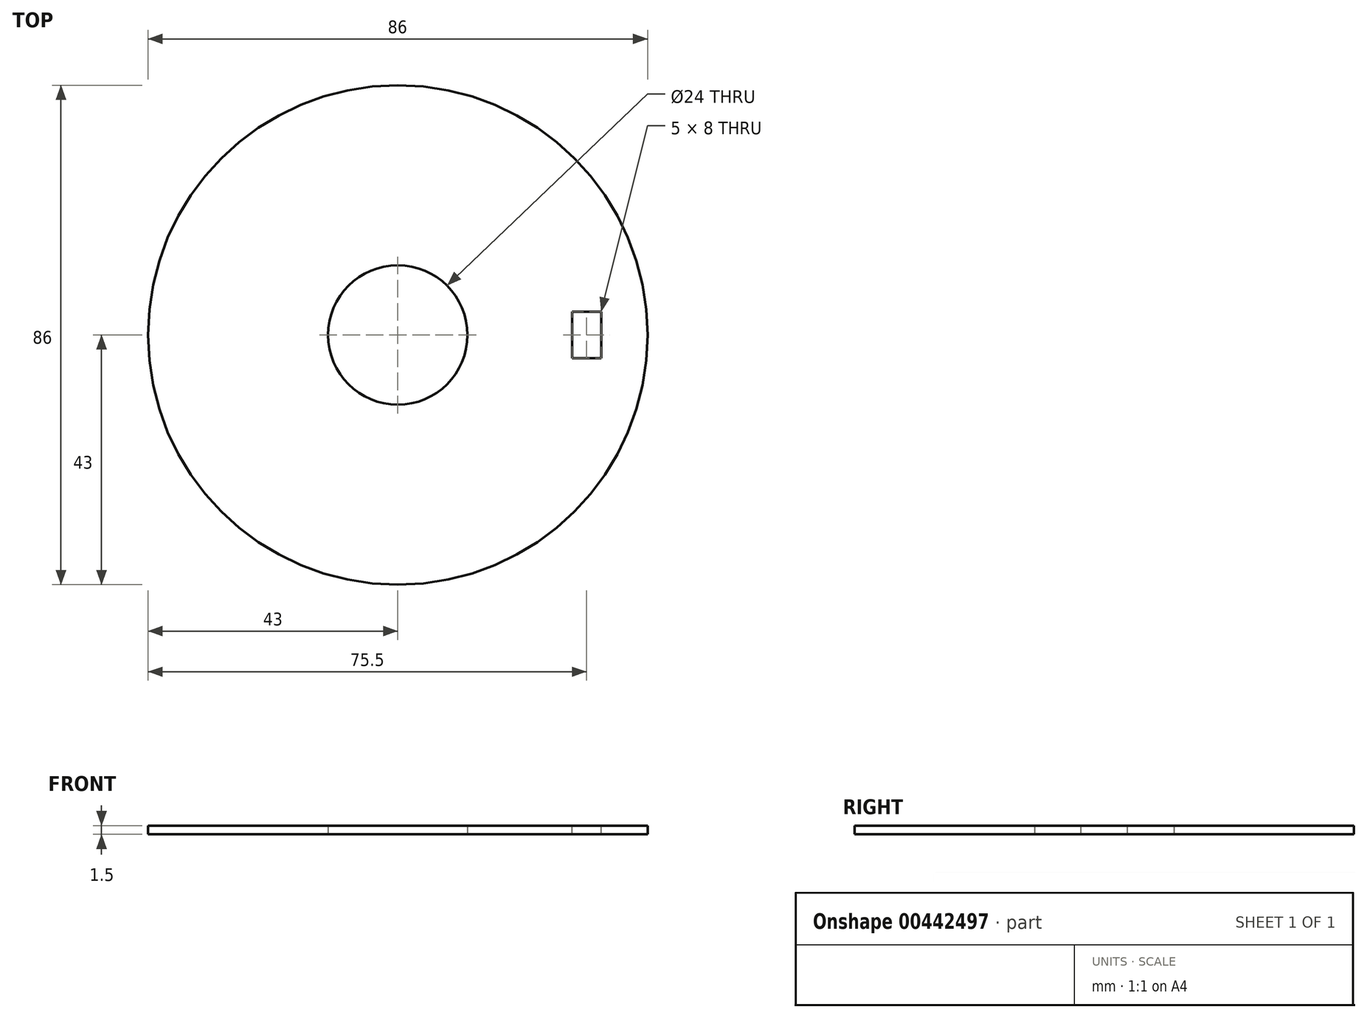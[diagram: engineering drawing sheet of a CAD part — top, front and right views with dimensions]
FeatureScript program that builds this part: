
annotation { "Feature Type Name" : "Feature", "Feature Type Description" : "" }
export const myFeature = defineFeature(function(context is Context, id is Id, definition is map)
    precondition{}
    {
        {
            var Q0;
            Q0=qCreatedBy(makeId("Top.planeOp"),FACE);
            var sketch = newSketch(context, id + "F0", { "sketchPlane" : qUnion([Q0])});
            skCircle(sketch, "E0", {"center": v(0, 0) * mm, "radius": 43 * mm});
            skCircle(sketch, "E1", {"center": v(0, 0) * mm, "radius": 12 * mm});
            skSolve(sketch);
        }
        {
            var Q0;
            Q0=makeQuery(id+"F0.imprint","IMPRINT",FACE,{"disambiguationData":[TD([[makeQuery(id+"F0.imprint","IMPRINT",EDGE,{"derivedFrom":sQuery(id+"F0.wireOp",EDGE,"E0")}),1.0]])]});
            extrude(context, id + "F1", {"entities" : qUnion([Q0]), "depth" : 1.5 * mm});
        }
        {
            var Q0;
            Q0=makeQuery(id+"F1.opExtrude","CAP_FACE",FACE,{"disambiguationData":[OSD([sQuery(id+"F0.wireOp",EDGE,"E0"),sQuery(id+"F0.wireOp",EDGE,"E1")])],"isStart":false});
            var sketch = newSketch(context, id + "F2", { "sketchPlane" : qUnion([Q0])});
            skLineSegment(sketch, "E2.bottom", {"start": v(30, 4) * mm, "end": v(35, 4) * mm});
            skLineSegment(sketch, "E2.top", {"start": v(30, -4) * mm, "end": v(35, -4) * mm});
            skLineSegment(sketch, "E2.left", {"start": v(35, 4) * mm, "end": v(35, -4) * mm});
            skLineSegment(sketch, "E2.right", {"start": v(30, 4) * mm, "end": v(30, -4) * mm});
            skSolve(sketch);
        }
        {
            var Q0;
            Q0 = qSketchRegion(id + "F2", true);
            extrude(context, id + "F3", {"entities" : qUnion([Q0]), "operationType" : NewBodyOperationType.REMOVE, "endBound" : BoundingType.UP_TO_NEXT, "oppositeDirection" : true, "depth" : 25 * mm});
        }
    });
